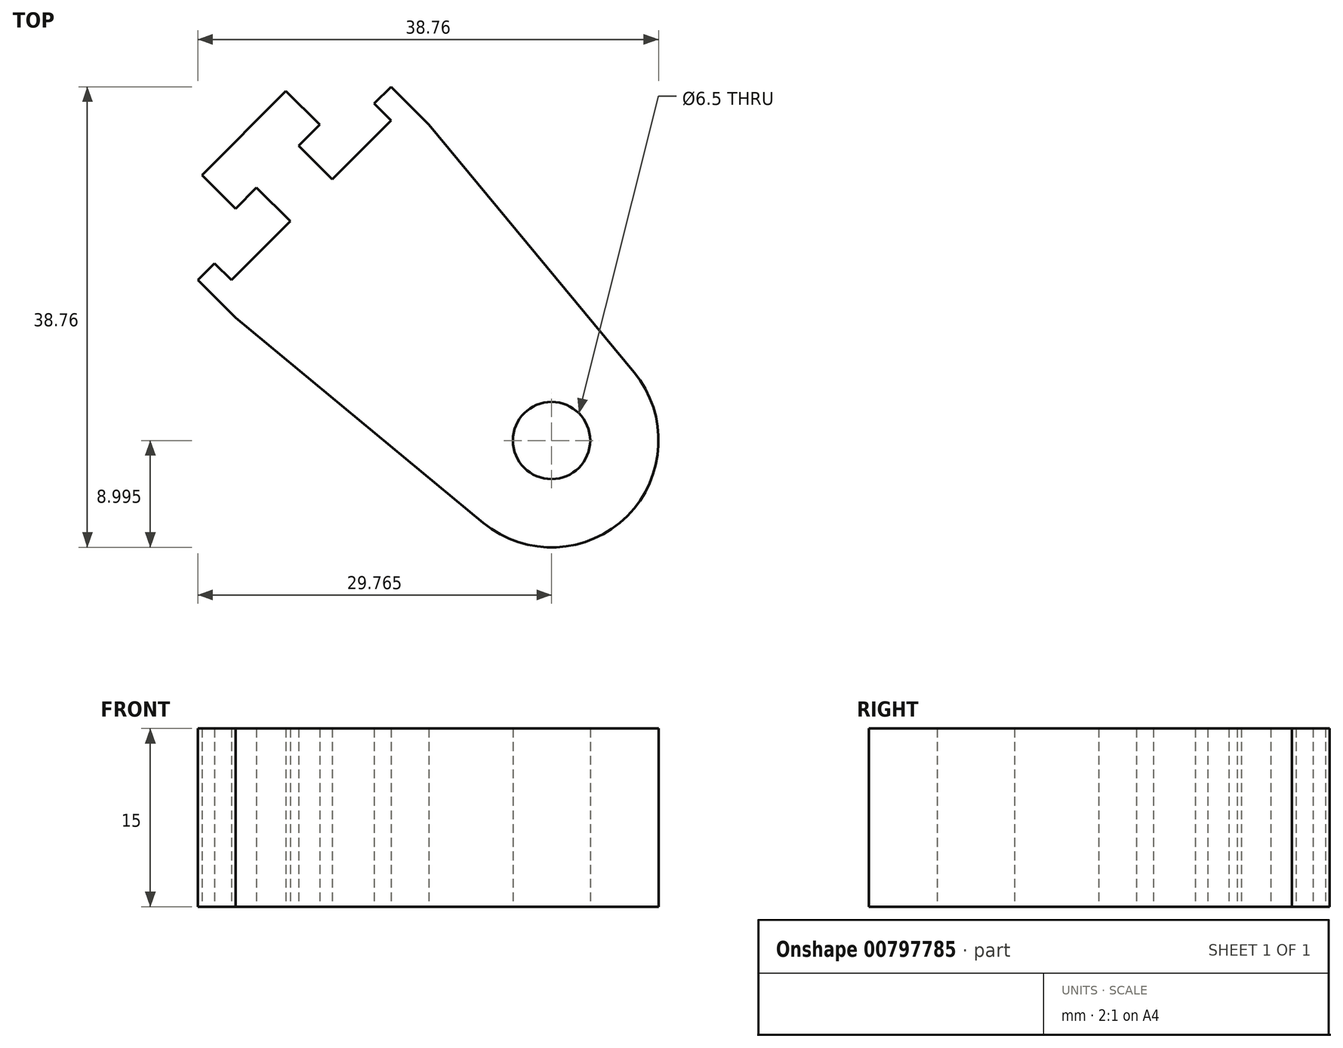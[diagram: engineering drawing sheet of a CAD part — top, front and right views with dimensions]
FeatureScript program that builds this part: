
annotation { "Feature Type Name" : "Feature", "Feature Type Description" : "" }
export const myFeature = defineFeature(function(context is Context, id is Id, definition is map)
    precondition{}
    {
        {
            var Q0;
            Q0=qCreatedBy(makeId("Front.planeOp"),FACE);
            var sketch = newSketch(context, id + "F0", { "sketchPlane" : qUnion([Q0])});
            skLineSegment(sketch, "E0", {"start": v(0, 0) * mm, "end": v(0, 78.33) * mm});
            skSolve(sketch);
        }
        {
            var Q0;
            Q0=sQuery(id+"F0.wireOp",EDGE,"E0");
            cPlane(context, id + "F1", {"entities" : qUnion([Q0]), "cplaneType" : CPlaneType.LINE_ANGLE, "offset" : 25 * mm, "angle" : 45 * degree, "width" : 150 * mm, "height" : 150 * mm});
        }
        {
            var Q0;
            Q0=qCreatedBy(makeId("Top.planeOp"),FACE);
            cPlane(context, id + "F2", {"entities" : qUnion([Q0]), "cplaneType" : CPlaneType.OFFSET, "offset" : 5 * mm, "width" : 150 * mm, "height" : 150 * mm});
        }
        {
            var Q0;
            Q0=qCreatedBy(id+"F2.planeOp",FACE);
            var sketch = newSketch(context, id + "F3", { "sketchPlane" : qUnion([Q0])});
            skLineSegment(sketch, "E1", {"start": v(100.4, -107.48) * mm, "end": v(107.48, -100.4) * mm});
            skLineSegment(sketch, "E2", {"start": v(107.48, -100.4) * mm, "end": v(110.3, -103.24) * mm});
            skLineSegment(sketch, "E3", {"start": v(110.3, -103.24) * mm, "end": v(108.54, -105) * mm});
            skLineSegment(sketch, "E4", {"start": v(108.54, -105) * mm, "end": v(111.37, -107.83) * mm});
            skLineSegment(sketch, "E5", {"start": v(111.37, -107.83) * mm, "end": v(116.32, -102.88) * mm});
            skLineSegment(sketch, "E6", {"start": v(116.32, -102.88) * mm, "end": v(114.9, -101.47) * mm});
            skLineSegment(sketch, "E7", {"start": v(114.9, -101.47) * mm, "end": v(116.32, -100.06) * mm});
            skLineSegment(sketch, "E8", {"start": v(116.32, -100.06) * mm, "end": v(119.5, -103.24) * mm});
            skLineSegment(sketch, "E9", {"start": v(119.5, -103.24) * mm, "end": v(136.76, -124.09) * mm});
            skArc(sketch, "E10", {"start": v(136.19, -136.19) * mm, "mid": v(138.81, -130.25) * mm, "end": v(136.76, -124.09) * mm});
            skLineSegment(sketch, "E11", {"start": v(136.19, -136.19) * mm, "end": v(153.23, -119.15) * mm, "construction": true});
            skLineSegment(sketch, "E12.MirrorCS", {"start": v(101.47, -114.9) * mm, "end": v(100.06, -116.32) * mm});
            skLineSegment(sketch, "E13.MirrorCS", {"start": v(102.88, -116.32) * mm, "end": v(101.47, -114.9) * mm});
            skLineSegment(sketch, "E14.MirrorCS", {"start": v(103.24, -110.3) * mm, "end": v(105, -108.54) * mm});
            skArc(sketch, "E15.MirrorCS", {"start": v(136.19, -136.19) * mm, "mid": v(130.25, -138.81) * mm, "end": v(124.09, -136.76) * mm});
            skLineSegment(sketch, "E16.MirrorCS", {"start": v(103.24, -119.5) * mm, "end": v(124.09, -136.76) * mm});
            skLineSegment(sketch, "E17.MirrorCS", {"start": v(100.06, -116.32) * mm, "end": v(103.24, -119.5) * mm});
            skLineSegment(sketch, "E18.MirrorCS", {"start": v(100.4, -107.48) * mm, "end": v(103.24, -110.3) * mm});
            skLineSegment(sketch, "E19.MirrorCS", {"start": v(105, -108.54) * mm, "end": v(107.83, -111.37) * mm});
            skLineSegment(sketch, "E20.MirrorCS", {"start": v(107.83, -111.37) * mm, "end": v(102.88, -116.32) * mm});
            skCircle(sketch, "E21", {"center": v(129.82, -129.82) * mm, "radius": 3.25 * mm});
            skLineSegment(sketch, "E22", {"start": v(129.82, -129.82) * mm, "end": v(97.2, -129.82) * mm, "construction": true});
            skLineSegment(sketch, "E23.MirrorCS", {"start": v(129.82, 129.82) * mm, "end": v(97.2, 129.82) * mm, "construction": true});
            skSolve(sketch);
        }
        {
            var Q0;
            Q0 = qSketchRegion(id + "F3", true);
            extrude(context, id + "F4", {"entities" : qUnion([Q0]), "depth" : 15 * mm, "offsetDistance" : 25 * mm});
        }
    });
